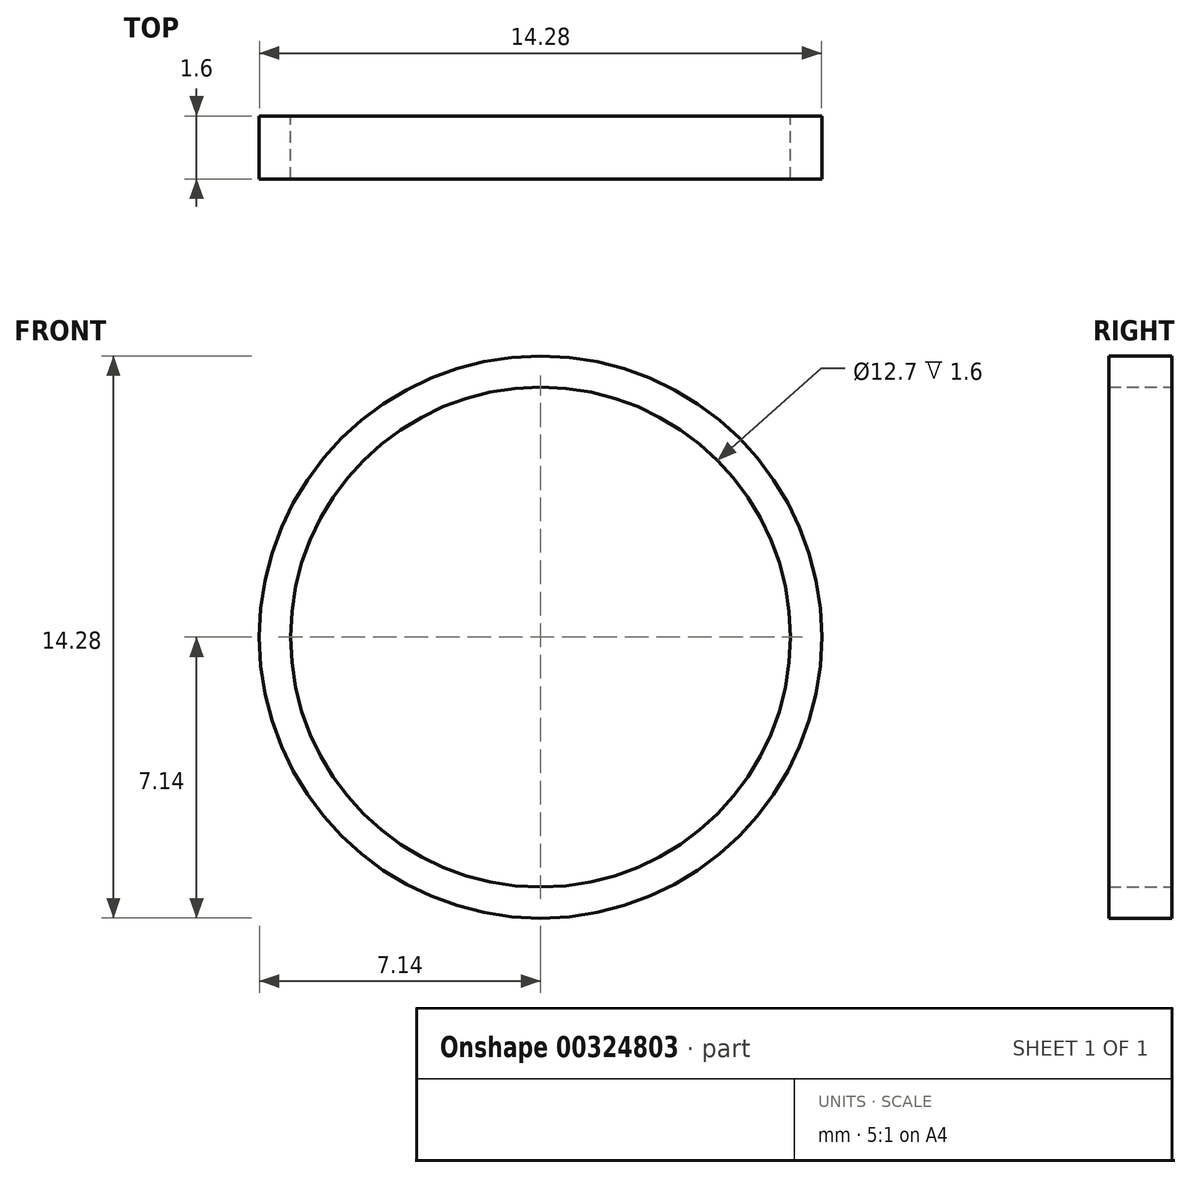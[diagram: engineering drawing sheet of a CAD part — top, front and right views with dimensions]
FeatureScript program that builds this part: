
annotation { "Feature Type Name" : "Feature", "Feature Type Description" : "" }
export const myFeature = defineFeature(function(context is Context, id is Id, definition is map)
    precondition{}
    {
        {
            var Q0;
            Q0=qCreatedBy(makeId("Front.planeOp"),FACE);
            var sketch = newSketch(context, id + "F0", { "sketchPlane" : qUnion([Q0])});
            skCircle(sketch, "E0", {"center": v(0, 0) * mm, "radius": 7.14 * mm});
            skCircle(sketch, "E1", {"center": v(0, 0) * mm, "radius": 6.35 * mm});
            skSolve(sketch);
        }
        {
            var Q0;
            Q0=makeQuery(id+"F0.imprint","IMPRINT",FACE,{"disambiguationData":[TD([[makeQuery(id+"F0.imprint","IMPRINT",EDGE,{"derivedFrom":sQuery(id+"F0.wireOp",EDGE,"E0")}),1.0]])]});
            extrude(context, id + "F1", {"entities" : qUnion([Q0]), "depth" : 1.6 * mm, "offsetDistance" : 25.4 * mm});
        }
    });
